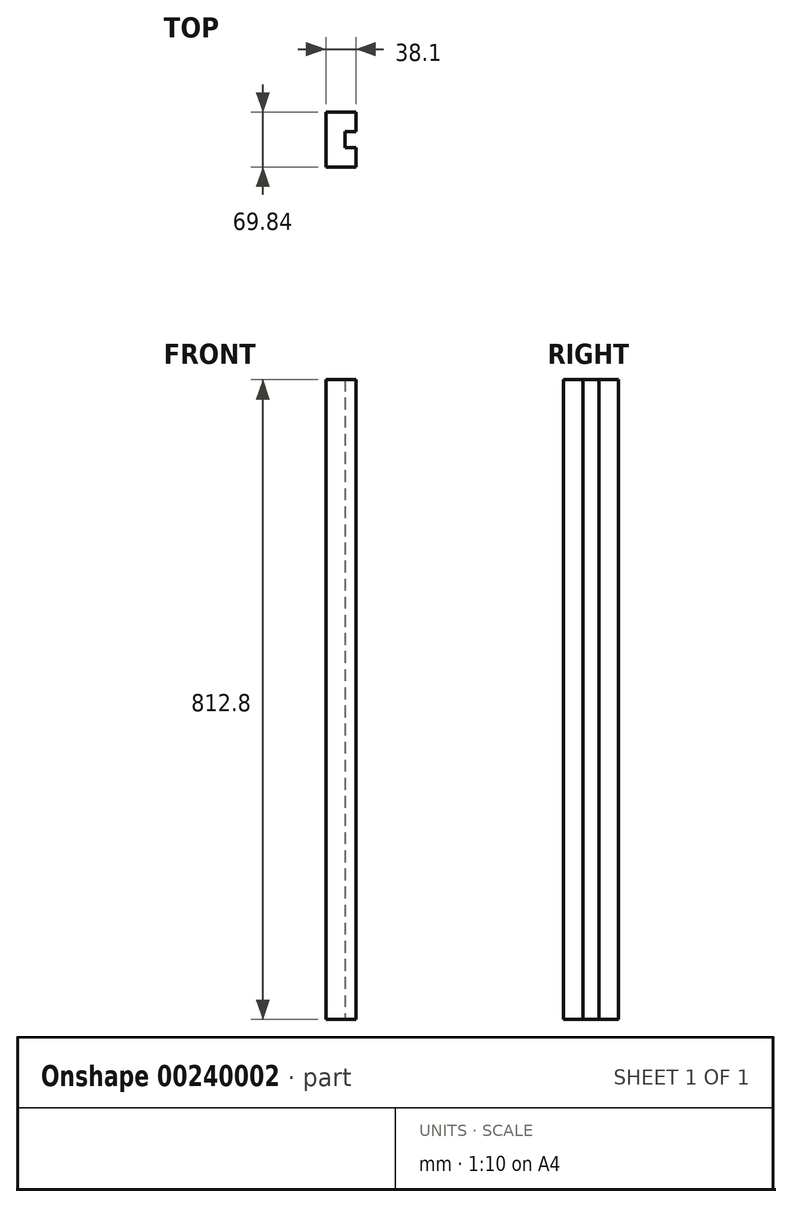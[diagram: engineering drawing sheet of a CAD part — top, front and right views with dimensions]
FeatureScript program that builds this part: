
annotation { "Feature Type Name" : "Feature", "Feature Type Description" : "" }
export const myFeature = defineFeature(function(context is Context, id is Id, definition is map)
    precondition{}
    {
        {
            var Q0;
            Q0=qCreatedBy(makeId("Top.planeOp"),FACE);
            var sketch = newSketch(context, id + "F0", { "sketchPlane" : qUnion([Q0])});
            skLineSegment(sketch, "E0", {"start": v(-38.1, -34.93) * mm, "end": v(-38.1, -10.32) * mm});
            skLineSegment(sketch, "E1", {"start": v(-38.1, -10.32) * mm, "end": v(-24.6, -10.32) * mm});
            skLineSegment(sketch, "E2", {"start": v(-24.6, -10.32) * mm, "end": v(-24.6, 10.32) * mm});
            skLineSegment(sketch, "E3", {"start": v(-24.6, 10.32) * mm, "end": v(-38.1, 10.32) * mm});
            skLineSegment(sketch, "E4", {"start": v(-38.1, 10.32) * mm, "end": v(-38.1, 34.92) * mm});
            skLineSegment(sketch, "E5", {"start": v(-38.1, 34.92) * mm, "end": v(38.1, 34.92) * mm});
            skLineSegment(sketch, "E6", {"start": v(38.1, 34.92) * mm, "end": v(38.1, 10.32) * mm});
            skLineSegment(sketch, "E7", {"start": v(38.1, 10.32) * mm, "end": v(24.6, 10.32) * mm});
            skLineSegment(sketch, "E8", {"start": v(24.6, 10.32) * mm, "end": v(24.6, -10.32) * mm});
            skLineSegment(sketch, "E9", {"start": v(24.6, -10.32) * mm, "end": v(38.1, -10.32) * mm});
            skLineSegment(sketch, "E10", {"start": v(38.1, -10.32) * mm, "end": v(38.1, -34.93) * mm});
            skLineSegment(sketch, "E11", {"start": v(38.1, -34.93) * mm, "end": v(-38.1, -34.93) * mm});
            skLineSegment(sketch, "E12", {"start": v(38.1, 34.93) * mm, "end": v(-38.1, -34.93) * mm, "construction": true});
            skLineSegment(sketch, "E13", {"start": v(-38.1, 34.93) * mm, "end": v(38.1, -34.93) * mm, "construction": true});
            skPoint(sketch, "E14", {"position": v(0, 0) * mm});
            skLineSegment(sketch, "E15", {"start": v(0, -34.93) * mm, "end": v(0, 34.92) * mm});
            skSolve(sketch);
        }
        {
            var Q0;
            {var subQ0=sQuery(id+"F0.wireOp",EDGE,"E6");Q0=makeQuery(id+"F0.imprint","IMPRINT",FACE,{"disambiguationData":[TD([[makeQuery(id+"F0.imprint","IMPRINT",EDGE,{"derivedFrom":subQ0}),-1.0]])]});}
            extrude(context, id + "F1", {"entities" : qUnion([Q0]), "depth" : 812.8 * mm, "offsetDistance" : 25.4 * mm});
        }
    });
